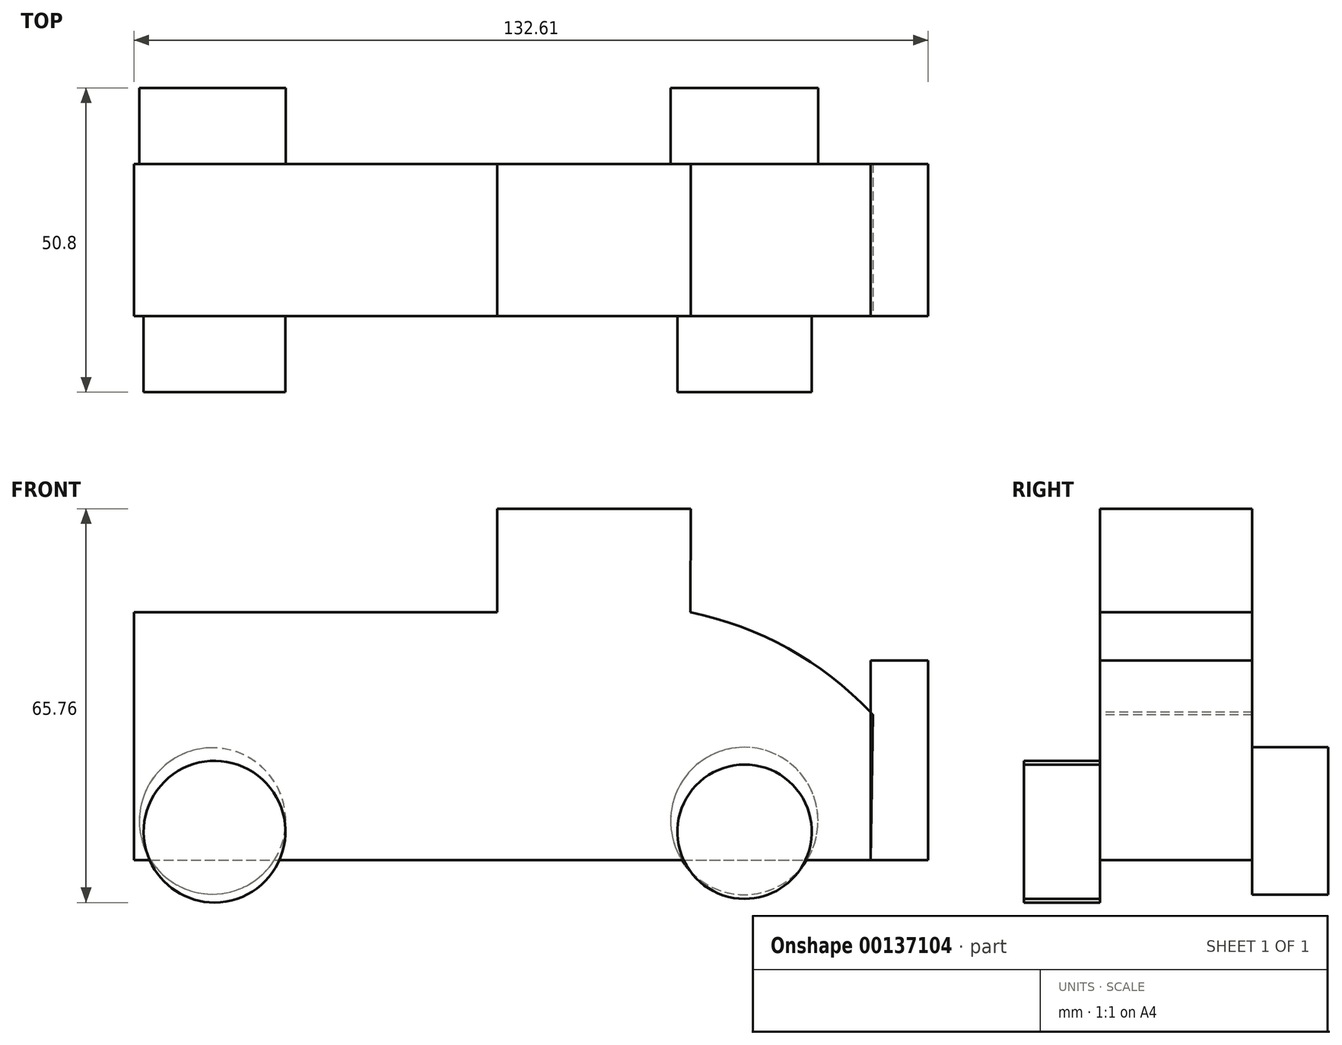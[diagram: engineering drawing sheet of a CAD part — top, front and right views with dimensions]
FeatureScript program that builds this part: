
annotation { "Feature Type Name" : "Feature", "Feature Type Description" : "" }
export const myFeature = defineFeature(function(context is Context, id is Id, definition is map)
    precondition{}
    {
        {
            var Q0;
            Q0=qCreatedBy(makeId("Front.planeOp"),FACE);
            var sketch = newSketch(context, id + "F0", { "sketchPlane" : qUnion([Q0])});
            skLineSegment(sketch, "E0", {"start": v(-77.03, 17.13) * mm, "end": v(-77.03, -24.3) * mm});
            skLineSegment(sketch, "E1", {"start": v(-77.03, -24.3) * mm, "end": v(45.95, -24.3) * mm});
            skLineSegment(sketch, "E2", {"start": v(-77.03, 17.13) * mm, "end": v(-16.4, 17.13) * mm});
            skArc(sketch, "E3", {"start": v(-16.4, 17.13) * mm, "mid": v(-0.26, -9.85) * mm, "end": v(15.89, 17.13) * mm});
            skArc(sketch, "E4", {"start": v(46.34, 0) * mm, "mid": v(32.45, 10.94) * mm, "end": v(15.89, 17.13) * mm});
            skLineSegment(sketch, "E5", {"start": v(46.34, 0) * mm, "end": v(45.95, -24.3) * mm});
            skLineSegment(sketch, "E6.bottom", {"start": v(45.95, -24.3) * mm, "end": v(55.58, -24.3) * mm});
            skLineSegment(sketch, "E6.top", {"start": v(45.95, 9.08) * mm, "end": v(55.58, 9.08) * mm});
            skLineSegment(sketch, "E6.left", {"start": v(45.95, -24.3) * mm, "end": v(45.95, 9.08) * mm});
            skLineSegment(sketch, "E6.right", {"start": v(55.58, -24.3) * mm, "end": v(55.58, 9.08) * mm});
            skCircle(sketch, "E7", {"center": v(-0.26, 8.47) * mm, "radius": 15.3 * mm});
            skLineSegment(sketch, "E8", {"start": v(-16.4, 17.13) * mm, "end": v(-16.4, 34.41) * mm});
            skLineSegment(sketch, "E9", {"start": v(-16.4, 34.41) * mm, "end": v(15.94, 34.41) * mm});
            skLineSegment(sketch, "E10", {"start": v(15.94, 34.41) * mm, "end": v(15.89, 17.13) * mm});
            skSolve(sketch);
        }
        {
            var Q0;
            Q0=makeQuery(id+"F0.imprint","IMPRINT",FACE,{"disambiguationData":[TD([[makeQuery(id+"F0.imprint","IMPRINT",EDGE,{"derivedFrom":sQuery(id+"F0.wireOp",EDGE,"E3")}),1.0]])]});
            var Q1;
            Q1=makeQuery(id+"F0.imprint","IMPRINT",FACE,{"disambiguationData":[TD([[makeQuery(id+"F0.imprint","IMPRINT",EDGE,{"derivedFrom":sQuery(id+"F0.wireOp",EDGE,"E0")}),1.0]])]});
            var Q2;
            {var subQ1=sQuery(id+"F0.wireOp",EDGE,"E5");Q2=makeQuery(id+"F0.imprint","IMPRINT",FACE,{"disambiguationData":[TD([[makeQuery(id+"F0.imprint","IMPRINT",EDGE,{"derivedFrom":subQ1}),1.0]])]});}
            var Q3;
            Q3=makeQuery(id+"F0.imprint","IMPRINT",FACE,{"disambiguationData":[TD([[makeQuery(id+"F0.imprint","IMPRINT",EDGE,{"derivedFrom":sQuery(id+"F0.wireOp",EDGE,"E7")}),1.0]])]});
            extrude(context, id + "F1", {"entities" : qUnion([Q0, Q1, Q2, Q3]), "oppositeDirection" : true, "depth" : 25.4 * mm});
        }
        {
            var Q0;
            Q0=qCreatedBy(makeId("Front.planeOp"),FACE);
            var sketch = newSketch(context, id + "F2", { "sketchPlane" : qUnion([Q0])});
            skCircle(sketch, "E11", {"center": v(-63.59, -19.52) * mm, "radius": 11.83 * mm});
            skCircle(sketch, "E12", {"center": v(24.91, -19.52) * mm, "radius": 11.22 * mm});
            skSolve(sketch);
        }
        {
            var Q0;
            Q0 = qSketchRegion(id + "F2", true);
            extrude(context, id + "F3", {"entities" : qUnion([Q0]), "operationType" : NewBodyOperationType.ADD, "depth" : 12.7 * mm});
        }
        {
            var Q0;
            Q0=makeQuery(id+"F1.opExtrude","CAP_FACE",FACE,{"disambiguationData":[OSD([sQuery(id+"F0.wireOp",EDGE,"E0"),sQuery(id+"F0.wireOp",EDGE,"E1"),sQuery(id+"F0.wireOp",EDGE,"E2"),sQuery(id+"F0.wireOp",EDGE,"E4"),sQuery(id+"F0.wireOp",EDGE,"E6.left"),sQuery(id+"F0.wireOp",EDGE,"E8"),sQuery(id+"F0.wireOp",EDGE,"E9"),sQuery(id+"F0.wireOp",EDGE,"E10")])],"isStart":false});
            var sketch = newSketch(context, id + "F4", { "sketchPlane" : qUnion([Q0])});
            skCircle(sketch, "E13", {"center": v(-24.87, -17.73) * mm, "radius": 12.3 * mm});
            skCircle(sketch, "E14", {"center": v(63.93, -17.73) * mm, "radius": 12.22 * mm});
            skSolve(sketch);
        }
        {
            var Q0;
            Q0 = qSketchRegion(id + "F4", true);
            extrude(context, id + "F5", {"entities" : qUnion([Q0]), "operationType" : NewBodyOperationType.ADD, "depth" : 12.7 * mm});
        }
    });
